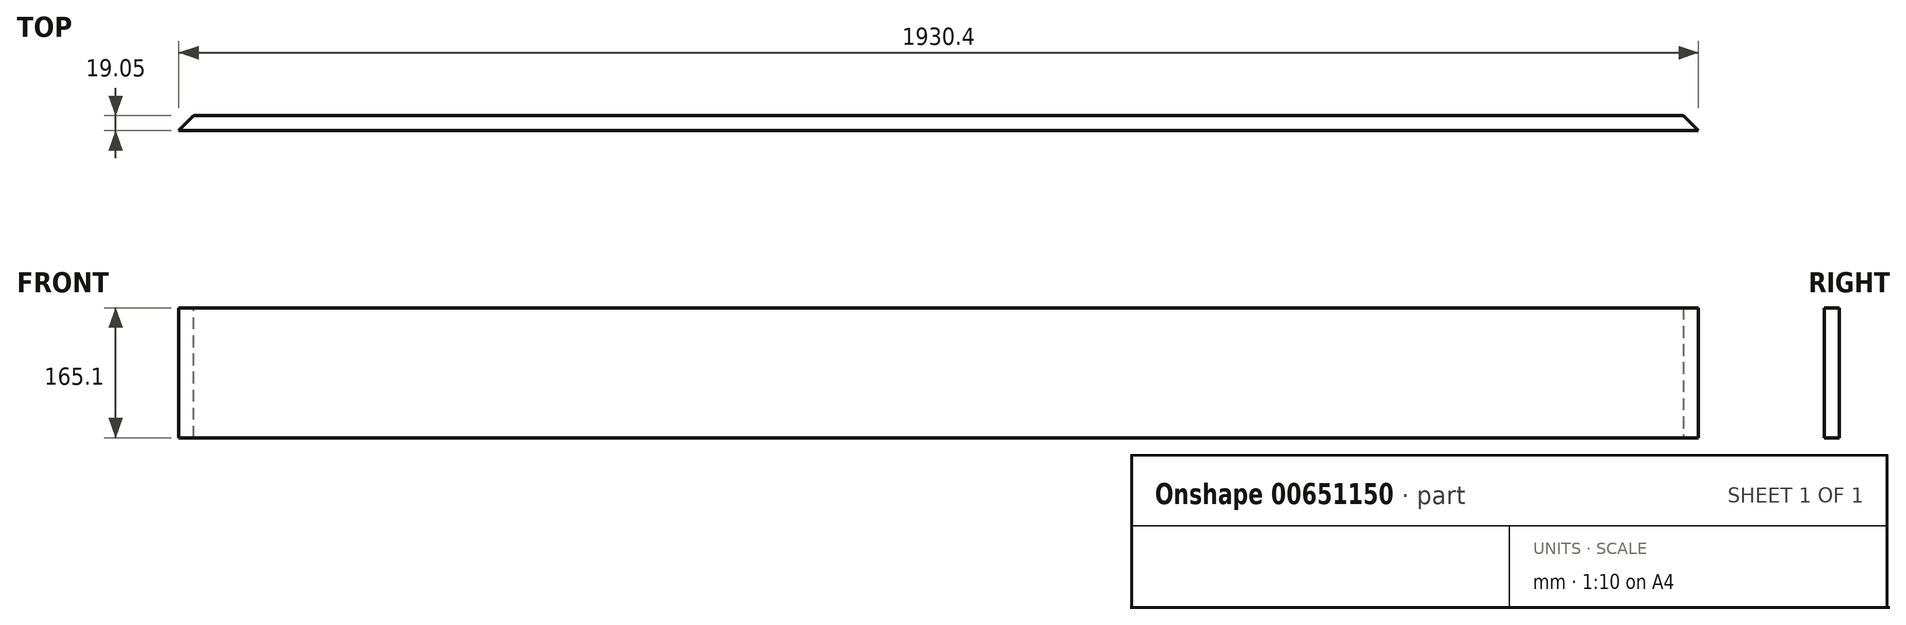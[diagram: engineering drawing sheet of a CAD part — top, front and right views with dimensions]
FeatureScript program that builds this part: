
annotation { "Feature Type Name" : "Feature", "Feature Type Description" : "" }
export const myFeature = defineFeature(function(context is Context, id is Id, definition is map)
    precondition{}
    {
        {
            var Q0;
            Q0=qCreatedBy(makeId("Front.planeOp"),FACE);
            var sketch = newSketch(context, id + "F0", { "sketchPlane" : qUnion([Q0])});
            skLineSegment(sketch, "E0.bottom", {"start": v(965.2, 82.55) * mm, "end": v(-965.2, 82.55) * mm});
            skLineSegment(sketch, "E0.top", {"start": v(965.2, -82.55) * mm, "end": v(-965.2, -82.55) * mm});
            skLineSegment(sketch, "E0.left", {"start": v(965.2, 82.55) * mm, "end": v(965.2, -82.55) * mm});
            skLineSegment(sketch, "E0.right", {"start": v(-965.2, 82.55) * mm, "end": v(-965.2, -82.55) * mm});
            skPoint(sketch, "E0.middle", {"position": v(0, 0) * mm});
            skSolve(sketch);
        }
        {
            var Q0;
            Q0 = qSketchRegion(id + "F0", true);
            extrude(context, id + "F1", {"entities" : qUnion([Q0]), "depth" : 19.05 * mm, "offsetDistance" : 25.4 * mm});
        }
        {
            var Q0;
            Q0=makeQuery(id+"F1.opExtrude","CAP_EDGE",EDGE,{"disambiguationData":[OSD([sQuery(id+"F0.wireOp",EDGE,"E0.left")])],"isStart":true});
            var Q1;
            Q1=makeQuery(id+"F1.opExtrude","CAP_EDGE",EDGE,{"disambiguationData":[OSD([sQuery(id+"F0.wireOp",EDGE,"E0.right")])],"isStart":true});
            chamfer(context, id + "F2", {"entities" : qUnion([Q0, Q1]), "width" : 19.05 * mm, "tangentPropagation" : true});
        }
    });
